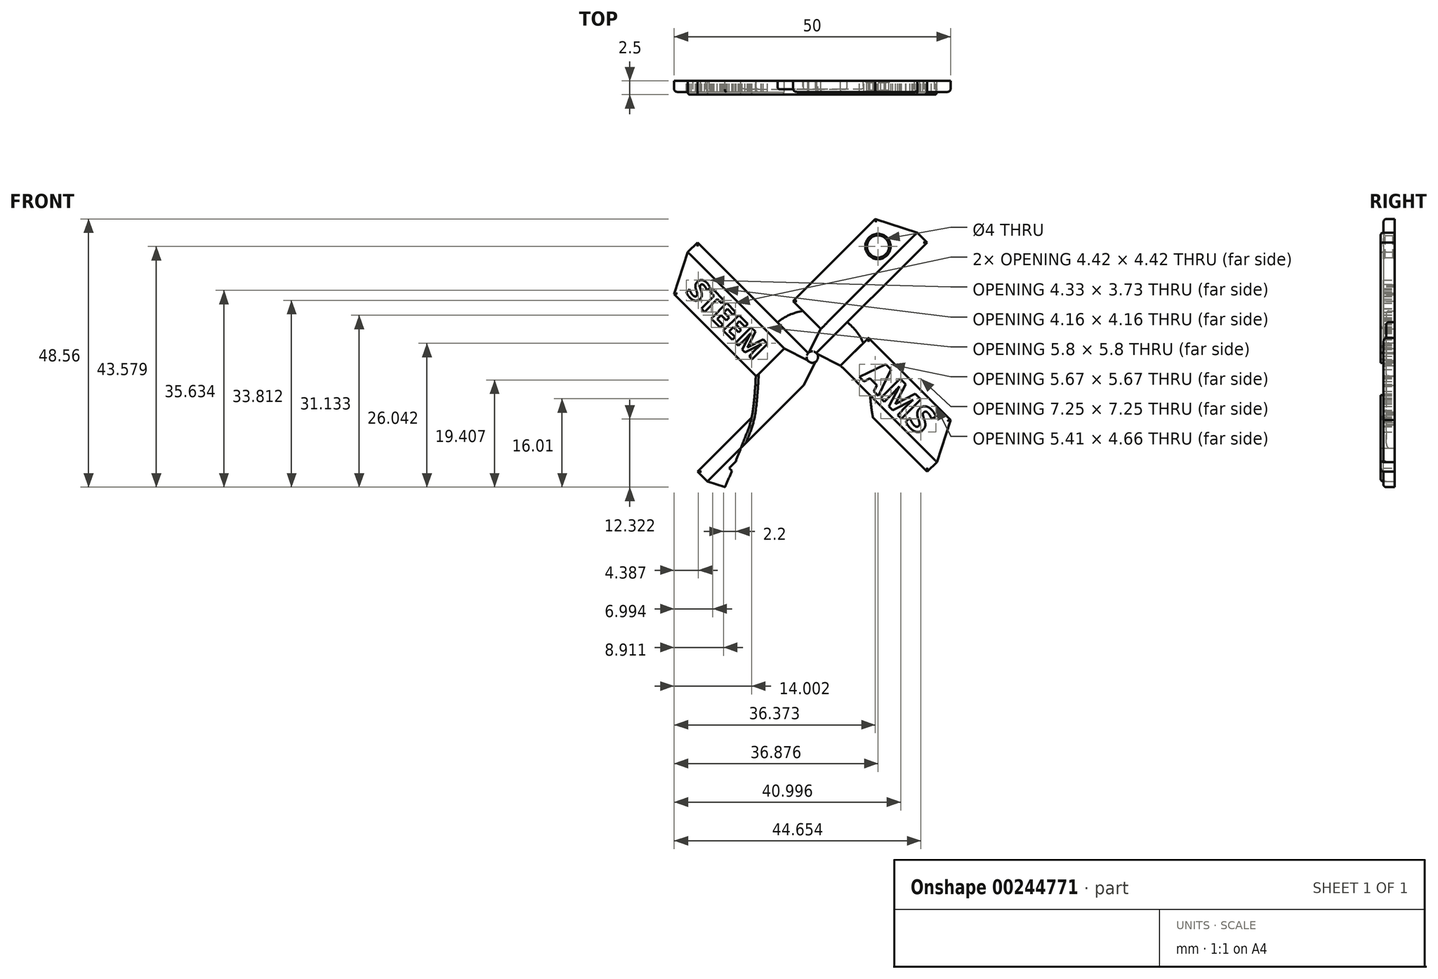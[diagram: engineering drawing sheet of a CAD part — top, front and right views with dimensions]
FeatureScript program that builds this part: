
annotation { "Feature Type Name" : "Feature", "Feature Type Description" : "" }
export const myFeature = defineFeature(function(context is Context, id is Id, definition is map)
    precondition{}
    {
        {
            var Q0;
            Q0=qCreatedBy(makeId("Front.planeOp"),FACE);
            var sketch = newSketch(context, id + "F0", { "sketchPlane" : qUnion([Q0])});
            skLineSegment(sketch, "E0.bottom", {"start": v(-25, 35) * mm, "end": v(25, 35) * mm, "construction": true});
            skLineSegment(sketch, "E0.top", {"start": v(-25, -35) * mm, "end": v(25, -35) * mm, "construction": true});
            skLineSegment(sketch, "E0.left", {"start": v(-25, 35) * mm, "end": v(-25, -35) * mm, "construction": true});
            skLineSegment(sketch, "E0.right", {"start": v(25, 35) * mm, "end": v(25, -35) * mm, "construction": true});
            skPoint(sketch, "E0.middle", {"position": v(0, 0) * mm});
            skLineSegment(sketch, "E1", {"start": v(0, -38.97) * mm, "end": v(0, 38.8) * mm, "construction": true});
            skPoint(sketch, "E1.endSnap0", {"position": v(0, 35) * mm});
            skFitSpline(sketch, "E2", {"points": [v(-23.9, -28.04) * mm, v(-12.4, -6.12) * mm, v(-10.15, 6.92) * mm], "startDerivative": vector(35.06, 43.89) * mm, "endDerivative": vector(3.09, 66.07) * mm});
            skLineSegment(sketch, "E3", {"start": v(-22.7, -35) * mm, "end": v(-20.44, -28.04) * mm});
            skLineSegment(sketch, "E4", {"start": v(-23.9, -28.04) * mm, "end": v(-20.44, -28.04) * mm});
            skFitSpline(sketch, "E5.MirrorCS", {"points": [v(23.9, -28.04) * mm, v(12.4, -6.12) * mm, v(10.15, 6.92) * mm], "startDerivative": vector(-35.06, 43.89) * mm, "endDerivative": vector(-3.09, 66.07) * mm});
            skLineSegment(sketch, "E6.MirrorCS", {"start": v(23.9, -28.04) * mm, "end": v(20.44, -28.04) * mm});
            skLineSegment(sketch, "E7.MirrorCS", {"start": v(22.7, -35) * mm, "end": v(20.44, -28.04) * mm});
            skPoint(sketch, "E8.end.orphan", {"position": v(0, -25.33) * mm});
            skPoint(sketch, "E9.MirrorCS.start.orphan", {"position": v(19.56, -25.33) * mm});
            skPoint(sketch, "E10.orphan", {"position": v(-19.56, -25.33) * mm});
            skLineSegment(sketch, "E11", {"start": v(-22.7, -35) * mm, "end": v(22.7, -35) * mm});
            skArc(sketch, "E12", {"start": v(9.24, 11.56) * mm, "mid": v(8, 13.61) * mm, "end": v(6.3, 15.3) * mm});
            skLineSegment(sketch, "E13", {"start": v(-0.73, 9.73) * mm, "end": v(-20.76, 29.76) * mm});
            skLineSegment(sketch, "E14", {"start": v(-20.76, 29.76) * mm, "end": v(-22.53, 28) * mm});
            skLineSegment(sketch, "E15", {"start": v(-22.53, 28) * mm, "end": v(-5.09, 10.55) * mm});
            skLineSegment(sketch, "E16", {"start": v(-22.53, 28) * mm, "end": v(-25, 20.38) * mm});
            skLineSegment(sketch, "E17", {"start": v(-25, 20.38) * mm, "end": v(-10.15, 5.53) * mm});
            skLineSegment(sketch, "E18", {"start": v(-10.15, 5.53) * mm, "end": v(-5.09, 10.55) * mm});
            skLineSegment(sketch, "E19", {"start": v(-5.09, 10.55) * mm, "end": v(-0.84, 8.4) * mm});
            skLineSegment(sketch, "E20.1.0", {"start": v(-0.73, 8.27) * mm, "end": v(-20.76, -11.76) * mm});
            skLineSegment(sketch, "E20.1.1", {"start": v(-19, -13.53) * mm, "end": v(-1.55, 3.91) * mm});
            skLineSegment(sketch, "E20.1.2", {"start": v(-19, -13.53) * mm, "end": v(-11.38, -16) * mm});
            skLineSegment(sketch, "E20.1.3", {"start": v(-20.76, -11.76) * mm, "end": v(-19, -13.53) * mm});
            skLineSegment(sketch, "E20.1.4", {"start": v(-11.38, -16) * mm, "end": v(3.47, -1.15) * mm});
            skLineSegment(sketch, "E20.1.5", {"start": v(3.47, -1.15) * mm, "end": v(-1.55, 3.91) * mm});
            skLineSegment(sketch, "E20.1.6", {"start": v(-1.55, 3.91) * mm, "end": v(0.6, 8.16) * mm});
            skLineSegment(sketch, "E20.2.0", {"start": v(0.73, 8.27) * mm, "end": v(20.76, -11.76) * mm});
            skLineSegment(sketch, "E20.2.1", {"start": v(22.53, -10) * mm, "end": v(5.09, 7.45) * mm});
            skLineSegment(sketch, "E20.2.2", {"start": v(22.53, -10) * mm, "end": v(25, -2.38) * mm});
            skLineSegment(sketch, "E20.2.3", {"start": v(20.76, -11.76) * mm, "end": v(22.53, -10) * mm});
            skLineSegment(sketch, "E20.2.4", {"start": v(25, -2.38) * mm, "end": v(10.15, 12.47) * mm});
            skLineSegment(sketch, "E20.2.5", {"start": v(10.15, 12.47) * mm, "end": v(5.09, 7.45) * mm});
            skLineSegment(sketch, "E20.2.6", {"start": v(5.09, 7.45) * mm, "end": v(0.84, 9.6) * mm});
            skLineSegment(sketch, "E20.3.0", {"start": v(0.73, 9.73) * mm, "end": v(20.76, 29.76) * mm});
            skLineSegment(sketch, "E20.3.1", {"start": v(19, 31.53) * mm, "end": v(1.55, 14.09) * mm});
            skLineSegment(sketch, "E20.3.2", {"start": v(19, 31.53) * mm, "end": v(11.38, 34) * mm});
            skLineSegment(sketch, "E20.3.3", {"start": v(20.76, 29.76) * mm, "end": v(19, 31.53) * mm});
            skLineSegment(sketch, "E20.3.4", {"start": v(11.38, 34) * mm, "end": v(-3.47, 19.15) * mm});
            skLineSegment(sketch, "E20.3.5", {"start": v(-3.47, 19.15) * mm, "end": v(1.55, 14.09) * mm});
            skLineSegment(sketch, "E20.3.6", {"start": v(1.55, 14.09) * mm, "end": v(-0.6, 9.84) * mm});
            skPoint(sketch, "E20.center", {"position": v(0, 9) * mm});
            skCircle(sketch, "E21", {"center": v(0, 9) * mm, "radius": 1.04 * mm});
            skPoint(sketch, "E22.orphan", {"position": v(0, 10.04) * mm});
            skPoint(sketch, "E23.orphan", {"position": v(-1.04, 9) * mm});
            skPoint(sketch, "E24.orphan", {"position": v(0, 7.96) * mm});
            skPoint(sketch, "E25.orphan", {"position": v(1.04, 9) * mm});
            skArc(sketch, "E26.trimOffspring", {"start": v(-1.7, 17.36) * mm, "mid": v(-4.13, 16.63) * mm, "end": v(-6.3, 15.3) * mm});
            skFitSpline(sketch, "E27.trimOffspring", {"points": [v(-23.9, -28.04) * mm, v(-12.4, -6.12) * mm, v(-10.15, 6.92) * mm], "startDerivative": vector(35.06, 43.89) * mm, "endDerivative": vector(3.09, 66.07) * mm});
            skText(sketch, "E28", { "text": "STEEM", "fontName": "OpenSans-Bold.ttf"});
            skText(sketch, "E29", { "text": "FEST", "fontName": "OpenSans-Bold.ttf"});
            skText(sketch, "E30", { "text": "AMS", "fontName": "OpenSans-Bold.ttf"});
            skCircle(sketch, "E31", {"center": v(11.88, 29.02) * mm, "radius": 2 * mm});
            skFitSpline(sketch, "E32", {"points": [v(-9.31, -17.26) * mm, v(-6.83, -14.77) * mm, v(-6.88, -15.43) * mm, v(-6.95, -17.65) * mm, v(-4.57, -23.19) * mm, v(-3.7, -27.78) * mm, v(-6.53, -30.74) * mm, v(-6.57, -30.41) * mm, v(-5.99, -27.84) * mm, v(-9.37, -20.02) * mm, v(-9.31, -17.26) * mm]});
            skFitSpline(sketch, "E33", {"points": [v(3.8, -17.24) * mm, v(6.28, -14.75) * mm, v(6.24, -15.4) * mm, v(6.16, -17.63) * mm, v(8.55, -23.17) * mm, v(9.43, -27.76) * mm, v(6.59, -30.72) * mm, v(6.55, -30.4) * mm, v(7.13, -27.82) * mm, v(3.75, -20) * mm, v(3.8, -17.24) * mm]});
            skFitSpline(sketch, "E34", {"points": [v(-2.86, -14.72) * mm, v(-0.48, -12.6) * mm, v(-0.37, -13.1) * mm, v(-0.61, -14.73) * mm, v(-0.21, -17.64) * mm, v(2.78, -23.73) * mm, v(4.07, -27.5) * mm, v(3.64, -29.3) * mm, v(0.11, -33) * mm, v(0.1, -32.23) * mm, v(0.67, -30.25) * mm, v(0.55, -28.27) * mm, v(-2.94, -20.78) * mm, v(-3.92, -16.89) * mm, v(-2.86, -14.72) * mm]});
            const initialGuessF0  = {"E28": [-0.02309, 0.02077, 0.7071, -0.7071, 0.004], "E29": [-0.012, -0.01503, 0.7071, 0.7071, 0.005], "E30": [0.00854, 0.0054, 0.7071, -0.7071, 0.005]};
            skSetInitialGuess(sketch, initialGuessF0);
            skSolve(sketch);
        }
        {
            var Q0;
            {var subQ0=sQuery(id+"F0.wireOp",EDGE,"E2");Q0=makeQuery(id+"F0.imprint","IMPRINT",FACE,{"disambiguationData":[TD([[makeQuery(id+"F0.imprint","IMPRINT",EDGE,{"derivedFrom":subQ0}),-1.0]])]});}
            var Q1;
            {var subQ5=sQuery(id+"F0.wireOp",EDGE,"E18");Q1=makeQuery(id+"F0.imprint","IMPRINT",FACE,{"disambiguationData":[TD([[makeQuery(id+"F0.imprint","IMPRINT",EDGE,{"derivedFrom":subQ5}),-1.0]])]});}
            var Q2;
            {var subQ3=sQuery(id+"F0.wireOp",EDGE,"E20.3.6");Q2=makeQuery(id+"F0.imprint","IMPRINT",FACE,{"disambiguationData":[TD([[makeQuery(id+"F0.imprint","IMPRINT",EDGE,{"derivedFrom":subQ3}),-1.0]])]});}
            var Q3;
            {var subQ1=sQuery(id+"F0.wireOp",EDGE,"E12");Q3=makeQuery(id+"F0.imprint","IMPRINT",FACE,{"disambiguationData":[TD([[makeQuery(id+"F0.imprint","IMPRINT",EDGE,{"derivedFrom":subQ1}),1.0]])]});}
            extrude(context, id + "F1", {"entities" : qUnion([Q0, Q1, Q2, Q3]), "depth" : 1.5 * mm});
        }
        {
            var Q0;
            {var subQ2=sQuery(id+"F0.wireOp",EDGE,"E20.1.1");Q0=makeQuery(id+"F0.imprint","IMPRINT",FACE,{"disambiguationData":[TD([[makeQuery(id+"F0.imprint","IMPRINT",EDGE,{"derivedFrom":subQ2}),-1.0]])]});}
            var Q1;
            {var subQ3=sQuery(id+"F0.wireOp",EDGE,"E20.2.1");Q1=makeQuery(id+"F0.imprint","IMPRINT",FACE,{"disambiguationData":[TD([[makeQuery(id+"F0.imprint","IMPRINT",EDGE,{"derivedFrom":subQ3}),-1.0]])]});}
            var Q2;
            {var subQ1=sQuery(id+"F0.wireOp",EDGE,"E20.3.1");Q2=makeQuery(id+"F0.imprint","IMPRINT",FACE,{"disambiguationData":[TD([[makeQuery(id+"F0.imprint","IMPRINT",EDGE,{"derivedFrom":subQ1}),-1.0]])]});}
            var Q3;
            Q3=makeQuery(id+"F0.imprint","IMPRINT",FACE,{"disambiguationData":[TD([[makeQuery(id+"F0.imprint","IMPRINT",EDGE,{"derivedFrom":sQuery(id+"F0.wireOp",EDGE,"E15")}),-1.0]])]});
            extrude(context, id + "F2", {"entities" : qUnion([Q0, Q1, Q2, Q3]), "depth" : 2 * mm});
        }
        {
            var Q0;
            Q0=makeQuery(id+"F0.imprint","IMPRINT",FACE,{"disambiguationData":[TD([[makeQuery(id+"F0.imprint","IMPRINT",EDGE,{"derivedFrom":sQuery(id+"F0.wireOp",EDGE,"E20.3.1")}),1.0]])]});
            var Q1;
            {var subQ0=sQuery(id+"F0.wireOp",EDGE,"E14");Q1=makeQuery(id+"F0.imprint","IMPRINT",FACE,{"disambiguationData":[TD([[makeQuery(id+"F0.imprint","IMPRINT",EDGE,{"derivedFrom":subQ0}),1.0]])]});}
            var Q2;
            Q2=makeQuery(id+"F0.imprint","IMPRINT",FACE,{"disambiguationData":[TD([[makeQuery(id+"F0.imprint","IMPRINT",EDGE,{"derivedFrom":sQuery(id+"F0.wireOp",EDGE,"E20.1.1")}),1.0]])]});
            var Q3;
            Q3=makeQuery(id+"F0.imprint","IMPRINT",FACE,{"disambiguationData":[TD([[makeQuery(id+"F0.imprint","IMPRINT",EDGE,{"derivedFrom":sQuery(id+"F0.wireOp",EDGE,"E20.2.1")}),1.0]])]});
            var Q4;
            {var subQ0=sQuery(id+"F0.wireOp",EDGE,"E21");var subQ5=makeQuery(id+"F0.imprint","INTERSECT",VERTEX,{"derivedFrom":[sQuery(id+"F0.wireOp",EDGE,"E20.2.6"),subQ0]});Q4=makeQuery(id+"F0.imprint","IMPRINT",FACE,{"disambiguationData":[TD([[makeQuery(id+"F0.imprint","IMPRINT",EDGE,{"disambiguationData":[TD([[subQ5,-1.0]])],"derivedFrom":subQ0}),1.0]])]});}
            extrude(context, id + "F3", {"entities" : qUnion([Q0, Q1, Q2, Q3, Q4]), "depth" : 2.5 * mm});
        }
        {
            var Q0;
            Q0=makeQuery(id+"F2.opExtrude","CAP_EDGE",EDGE,{"disambiguationData":[OSD([sQuery(id+"F0.wireOp",EDGE,"E31")])],"isStart":false});
            var Q1;
            Q1=makeQuery(id+"F2.opExtrude","CAP_EDGE",EDGE,{"disambiguationData":[OSD([sQuery(id+"F0.wireOp",EDGE,"E31")])],"isStart":true});
            chamfer(context, id + "F4", {"entities" : qUnion([Q0, Q1]), "width" : .3 * mm, "tangentPropagation" : true});
        }
        {
            var Q0;
            Q0=makeQuery(id+"F2.opExtrude","CAP_EDGE",EDGE,{"disambiguationData":[OSD([sQuery(id+"F0.wireOp",EDGE,"E20.3.4")])],"isStart":false});
            var Q1;
            Q1=makeQuery(id+"F2.opExtrude","CAP_EDGE",EDGE,{"disambiguationData":[OSD([sQuery(id+"F0.wireOp",EDGE,"E20.3.2")])],"isStart":false});
            var Q2;
            Q2=makeQuery(id+"F2.opExtrude","CAP_EDGE",EDGE,{"disambiguationData":[OSD([sQuery(id+"F0.wireOp",EDGE,"E20.3.5")])],"isStart":false});
            var Q3;
            Q3=makeQuery(id+"F3.opExtrude","CAP_EDGE",EDGE,{"disambiguationData":[OSD([sQuery(id+"F0.wireOp",EDGE,"E20.3.0")])],"isStart":false});
            var Q4;
            Q4=makeQuery(id+"F3.opExtrude","CAP_EDGE",EDGE,{"disambiguationData":[OSD([sQuery(id+"F0.wireOp",EDGE,"E20.3.3")])],"isStart":false});
            var Q5;
            Q5=makeQuery(id+"F1.opExtrude","CAP_EDGE",EDGE,{"disambiguationData":[OSD([sQuery(id+"F0.wireOp",EDGE,"E12")])],"isStart":false});
            var Q6;
            Q6=makeQuery(id+"F2.opExtrude","CAP_EDGE",EDGE,{"disambiguationData":[OSD([sQuery(id+"F0.wireOp",EDGE,"E20.2.4")])],"isStart":false});
            var Q7;
            Q7=makeQuery(id+"F2.opExtrude","CAP_EDGE",EDGE,{"disambiguationData":[OSD([sQuery(id+"F0.wireOp",EDGE,"E20.2.5")])],"isStart":false});
            var Q8;
            Q8=makeQuery(id+"F2.opExtrude","CAP_EDGE",EDGE,{"disambiguationData":[OSD([sQuery(id+"F0.wireOp",EDGE,"E20.2.2")])],"isStart":false});
            var Q9;
            Q9=makeQuery(id+"F3.opExtrude","CAP_EDGE",EDGE,{"disambiguationData":[OSD([sQuery(id+"F0.wireOp",EDGE,"E20.2.3")])],"isStart":false});
            var Q10;
            Q10=makeQuery(id+"F3.opExtrude","CAP_EDGE",EDGE,{"disambiguationData":[OSD([sQuery(id+"F0.wireOp",EDGE,"E20.2.0")])],"isStart":false});
            var Q11;
            Q11=makeQuery(id+"F3.opExtrude","CAP_EDGE",EDGE,{"disambiguationData":[OSD([sQuery(id+"F0.wireOp",EDGE,"E20.1.6")])],"isStart":false});
            var Q12;
            Q12=makeQuery(id+"F2.opExtrude","CAP_EDGE",EDGE,{"disambiguationData":[OSD([sQuery(id+"F0.wireOp",EDGE,"E20.1.5")])],"isStart":false});
            var Q13;
            Q13=makeQuery(id+"F2.opExtrude","CAP_EDGE",EDGE,{"disambiguationData":[OSD([sQuery(id+"F0.wireOp",EDGE,"E20.1.4")])],"isStart":false});
            var Q14;
            Q14=makeQuery(id+"F2.opExtrude","CAP_EDGE",EDGE,{"disambiguationData":[OSD([sQuery(id+"F0.wireOp",EDGE,"E20.1.2")])],"isStart":false});
            var Q15;
            Q15=makeQuery(id+"F3.opExtrude","CAP_EDGE",EDGE,{"disambiguationData":[OSD([sQuery(id+"F0.wireOp",EDGE,"E20.1.3")])],"isStart":false});
            var Q16;
            Q16=makeQuery(id+"F3.opExtrude","CAP_EDGE",EDGE,{"disambiguationData":[OSD([sQuery(id+"F0.wireOp",EDGE,"E20.1.0")])],"isStart":false});
            var Q17;
            Q17=makeQuery(id+"F3.opExtrude","CAP_EDGE",EDGE,{"disambiguationData":[OSD([sQuery(id+"F0.wireOp",EDGE,"E19")])],"isStart":false});
            var Q18;
            Q18=makeQuery(id+"F2.opExtrude","CAP_EDGE",EDGE,{"disambiguationData":[OSD([sQuery(id+"F0.wireOp",EDGE,"E17")])],"isStart":false});
            var Q19;
            Q19=makeQuery(id+"F2.opExtrude","CAP_EDGE",EDGE,{"disambiguationData":[OSD([sQuery(id+"F0.wireOp",EDGE,"E16")])],"isStart":false});
            var Q20;
            Q20=makeQuery(id+"F3.opExtrude","CAP_EDGE",EDGE,{"disambiguationData":[OSD([sQuery(id+"F0.wireOp",EDGE,"E14")])],"isStart":false});
            var Q21;
            Q21=makeQuery(id+"F3.opExtrude","CAP_EDGE",EDGE,{"disambiguationData":[OSD([sQuery(id+"F0.wireOp",EDGE,"E13")])],"isStart":false});
            var Q22;
            Q22=makeQuery(id+"F3.opExtrude","CAP_EDGE",EDGE,{"disambiguationData":[OSD([sQuery(id+"F0.wireOp",EDGE,"E20.3.6")])],"isStart":false});
            var Q23;
            Q23=makeQuery(id+"F1.opExtrude","CAP_EDGE",EDGE,{"disambiguationData":[OSD([sQuery(id+"F0.wireOp",EDGE,"E26.trimOffspring")])],"isStart":false});
            var Q24;
            Q24=makeQuery(id+"F1.opExtrude","CAP_EDGE",EDGE,{"disambiguationData":[OSD([sQuery(id+"F0.wireOp",EDGE,"E27.trimOffspring")])],"isStart":false});
            var Q25;
            Q25=makeQuery(id+"F1.opExtrude","CAP_EDGE",EDGE,{"disambiguationData":[OSD([sQuery(id+"F0.wireOp",EDGE,"E2")])],"isStart":false});
            var Q26;
            Q26=makeQuery(id+"F1.opExtrude","CAP_EDGE",EDGE,{"disambiguationData":[OSD([sQuery(id+"F0.wireOp",EDGE,"E4")])],"isStart":false});
            var Q27;
            Q27=makeQuery(id+"F1.opExtrude","CAP_EDGE",EDGE,{"disambiguationData":[OSD([sQuery(id+"F0.wireOp",EDGE,"E3")])],"isStart":false});
            var Q28;
            Q28=makeQuery(id+"F1.opExtrude","CAP_EDGE",EDGE,{"disambiguationData":[OSD([sQuery(id+"F0.wireOp",EDGE,"E11")])],"isStart":false});
            var Q29;
            Q29=makeQuery(id+"F1.opExtrude","CAP_EDGE",EDGE,{"disambiguationData":[OSD([sQuery(id+"F0.wireOp",EDGE,"E7.MirrorCS")])],"isStart":false});
            var Q30;
            Q30=makeQuery(id+"F1.opExtrude","CAP_EDGE",EDGE,{"disambiguationData":[OSD([sQuery(id+"F0.wireOp",EDGE,"E6.MirrorCS")])],"isStart":false});
            var Q31;
            Q31=makeQuery(id+"F1.opExtrude","CAP_EDGE",EDGE,{"disambiguationData":[OSD([sQuery(id+"F0.wireOp",EDGE,"E5.MirrorCS")])],"isStart":false});
            var Q32;
            Q32=makeQuery(id+"F3.opExtrude","CAP_EDGE",EDGE,{"disambiguationData":[OSD([sQuery(id+"F0.wireOp",EDGE,"E20.2.6")])],"isStart":false});
            var Q33;
            Q33=makeQuery(id+"F1.opExtrude","CAP_EDGE",EDGE,{"disambiguationData":[OSD([sQuery(id+"F0.wireOp",EDGE,"E32")])],"isStart":false});
            var Q34;
            Q34=makeQuery(id+"F1.opExtrude","CAP_EDGE",EDGE,{"disambiguationData":[OSD([sQuery(id+"F0.wireOp",EDGE,"E34")])],"isStart":false});
            var Q35;
            Q35=makeQuery(id+"F1.opExtrude","CAP_EDGE",EDGE,{"disambiguationData":[OSD([sQuery(id+"F0.wireOp",EDGE,"E33")])],"isStart":false});
            fillet(context, id + "F5", {"entities" : qUnion([Q0, Q1, Q2, Q3, Q4, Q5, Q6, Q7, Q8, Q9, Q10, Q11, Q12, Q13, Q14, Q15, Q16, Q17, Q18, Q19, Q20, Q21, Q22, Q23, Q24, Q25, Q26, Q27, Q28, Q29, Q30, Q31, Q32, Q33, Q34, Q35]), "radius" : .5 * mm, "tangentPropagation" : true, "allowEdgeOverflow" : false});
        }
    });
